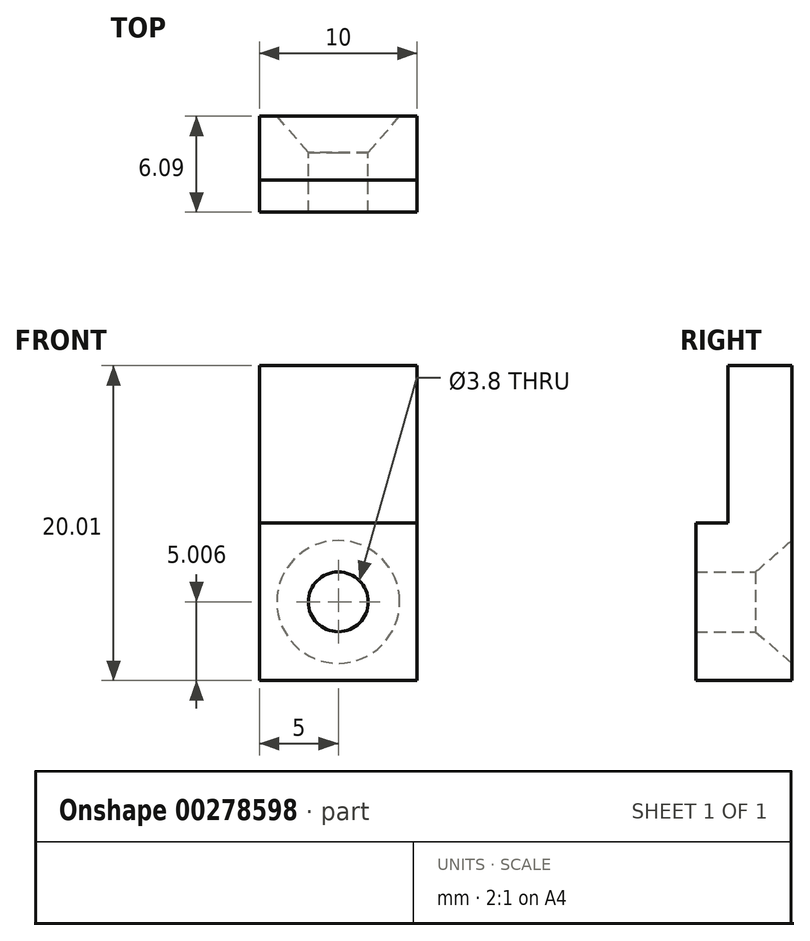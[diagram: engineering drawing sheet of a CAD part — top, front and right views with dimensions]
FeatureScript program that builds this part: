
annotation { "Feature Type Name" : "Feature", "Feature Type Description" : "" }
export const myFeature = defineFeature(function(context is Context, id is Id, definition is map)
    precondition{}
    {
        {
            var Q0;
            Q0=qCreatedBy(makeId("Front.planeOp"),FACE);
            var sketch = newSketch(context, id + "F0", { "sketchPlane" : qUnion([Q0])});
            skLineSegment(sketch, "E0.bottom", {"start": v(-5, 11.83) * mm, "end": v(5, 11.83) * mm});
            skLineSegment(sketch, "E0.top", {"start": v(-5, -8.18) * mm, "end": v(5, -8.18) * mm});
            skLineSegment(sketch, "E0.left", {"start": v(-5, 11.82) * mm, "end": v(-5, -8.18) * mm});
            skLineSegment(sketch, "E0.right", {"start": v(5, 11.83) * mm, "end": v(5, -8.18) * mm});
            skPoint(sketch, "E1", {"position": v(0, 0) * mm});
            skPoint(sketch, "E2", {"position": v(5, 1.83) * mm});
            skPoint(sketch, "E3", {"position": v(-5, 1.82) * mm});
            skLineSegment(sketch, "E4", {"start": v(5, 1.83) * mm, "end": v(-5, 1.82) * mm});
            skSolve(sketch);
        }
        {
            var Q0;
            {var subQ0=sQuery(id+"F0.wireOp",EDGE,"E0.top");Q0=makeQuery(id+"F0.imprint","IMPRINT",FACE,{"disambiguationData":[TD([[makeQuery(id+"F0.imprint","IMPRINT",EDGE,{"derivedFrom":subQ0}),1.0]])]});}
            extrude(context, id + "F1", {"entities" : qUnion([Q0]), "depth" : 2.03 * mm});
        }
        {
            var Q0;
            {var subQ0=sQuery(id+"F0.wireOp",EDGE,"E0.bottom");Q0=makeQuery(id+"F0.imprint","IMPRINT",FACE,{"disambiguationData":[TD([[makeQuery(id+"F0.imprint","IMPRINT",EDGE,{"derivedFrom":subQ0}),-1.0]])]});}
            var Q1;
            {var subQ0=sQuery(id+"F0.wireOp",EDGE,"E0.top");Q1=makeQuery(id+"F0.imprint","IMPRINT",FACE,{"disambiguationData":[TD([[makeQuery(id+"F0.imprint","IMPRINT",EDGE,{"derivedFrom":subQ0}),1.0]])]});}
            extrude(context, id + "F2", {"entities" : qUnion([Q0, Q1]), "operationType" : NewBodyOperationType.ADD, "oppositeDirection" : true, "depth" : 2.03 * mm * 2});
        }
        {
            var Q0;
            Q0=makeQuery(id+"F2.opExtrude","CAP_FACE",FACE,{"disambiguationData":[OSD([sQuery(id+"F0.wireOp",EDGE,"E0.bottom"),sQuery(id+"F0.wireOp",EDGE,"E0.top"),sQuery(id+"F0.wireOp",EDGE,"E0.left"),sQuery(id+"F0.wireOp",EDGE,"E0.right")])],"isStart":false});
            var sketch = newSketch(context, id + "F3", { "sketchPlane" : qUnion([Q0])});
            skPoint(sketch, "E5", {"position": v(0, -3.17) * mm});
            skSolve(sketch);
        }
        {
            var Q0;
            Q0=sQuery(id+"F3.wireOp",VERTEX,"E5");
            var Q1;
            Q1=makeQuery(id+"F1.opExtrude","SWEPT_BODY",BODY,{"disambiguationData":[OSD([sQuery(id+"F0.wireOp",EDGE,"E0.top"),sQuery(id+"F0.wireOp",EDGE,"E0.left"),sQuery(id+"F0.wireOp",EDGE,"E0.right"),sQuery(id+"F0.wireOp",EDGE,"UszvLyXm-xrY3-te1D-vuD3-KJPa3PtABHbh")])]});
            hole(context, id + "F4", {"style" : HoleStyle.C_SINK, "endStyle" : HoleEndStyle.THROUGH, "standardTappedOrClearance" : lookupTablePath({ "standard" : "ANSI", "fit" : "Normal (ASME)", "size" : "#6", "type" : "Clearance" }), "standardBlindInLast" : lookupTablePath({ "fit" : "Free", "standard" : "ANSI", "size" : "#6", "type" : "Clearance" }), "holeDiameter" : 3.8 * mm, "cSinkDiameter" : 7.8 * mm, "cSinkAngle" : 82 * degree, "tappedDepth" : 12 * mm, "tapClearance" : 3, "locations" : qUnion([Q0]), "scope" : qUnion([Q1])});
        }
    });
